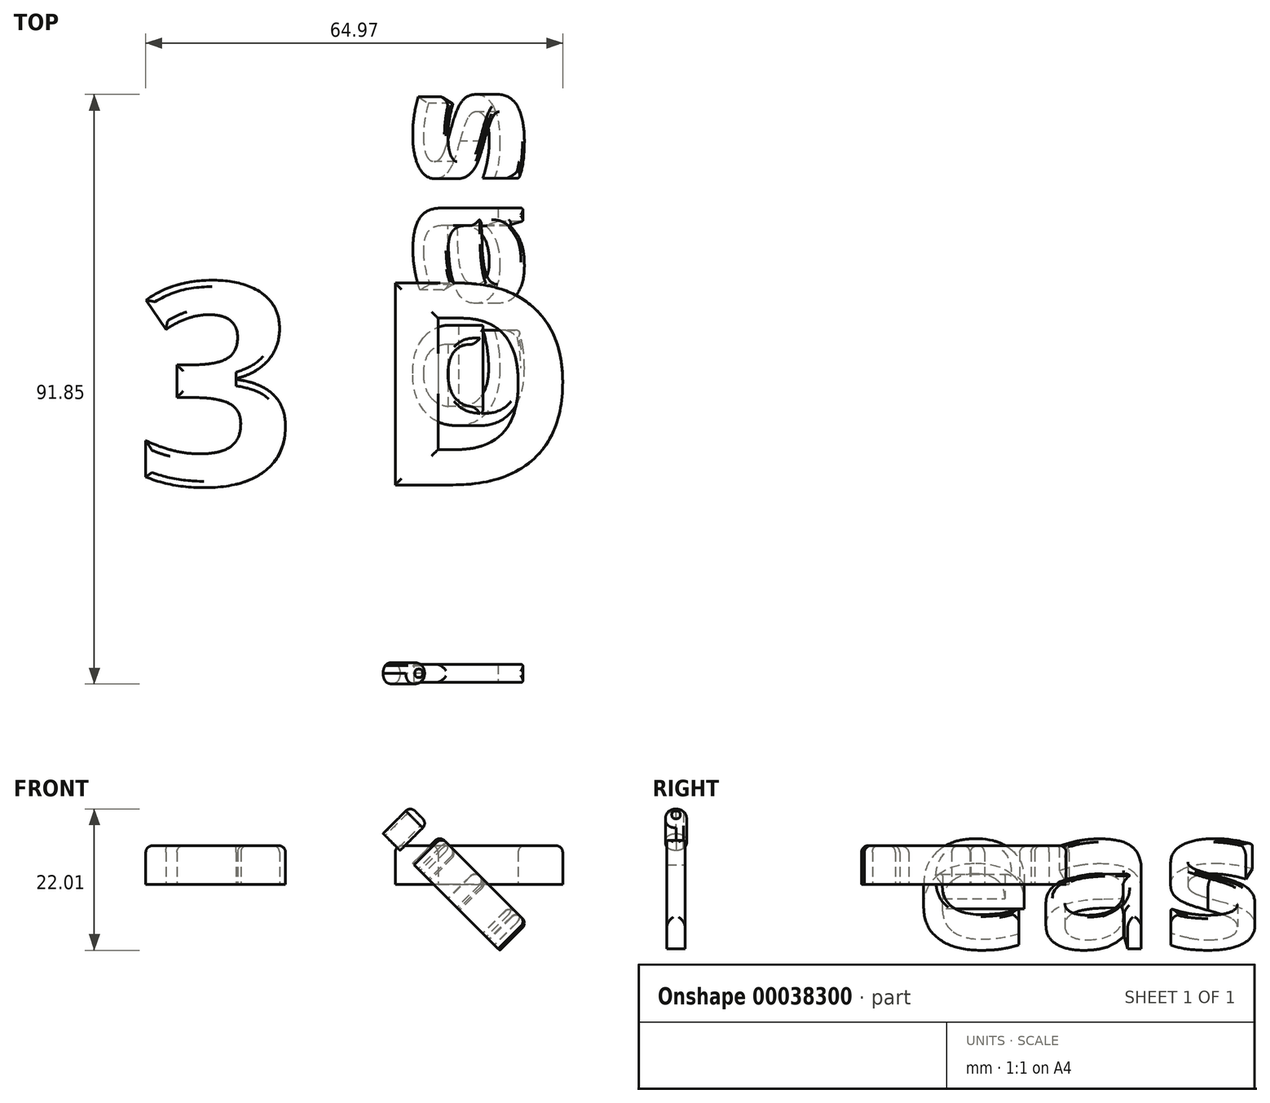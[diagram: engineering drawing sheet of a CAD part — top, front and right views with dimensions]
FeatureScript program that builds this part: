
annotation { "Feature Type Name" : "Feature", "Feature Type Description" : "" }
export const myFeature = defineFeature(function(context is Context, id is Id, definition is map)
    precondition{}
    {
        {
            var Q0;
            Q0=qCreatedBy(makeId("Top.planeOp"),FACE);
            var sketch = newSketch(context, id + "F0", { "sketchPlane" : qUnion([Q0])});
            skText(sketch, "E0", { "text": "3 D", "fontName": "OpenSans-Bold.ttf"});
            const initialGuessF0  = {"E0": [-0.06666, 0, 1, 0, 0.03172]};
            skSetInitialGuess(sketch, initialGuessF0);
            skSolve(sketch);
        }
        {
            var Q0;
            Q0=makeQuery(id+"F0.imprint","IMPRINT",FACE,{"disambiguationData":[TD([[makeQuery(id+"F0.imprint","IMPRINT",EDGE,{"derivedFrom":sQuery(id+"F0.wireOp",EDGE,"E0.sketch_text.stroke-0")}),-1.0]])]});
            var Q1;
            Q1=makeQuery(id+"F0.imprint","IMPRINT",FACE,{"disambiguationData":[TD([[makeQuery(id+"F0.imprint","IMPRINT",EDGE,{"derivedFrom":sQuery(id+"F0.wireOp",EDGE,"1949aad5-839d-4fb3-a845-ca18cb88f10a.sketch_text.stroke-0")}),-1.0]])]});
            var Q2;
            Q2=makeQuery(id+"F0.imprint","IMPRINT",FACE,{"disambiguationData":[TD([[makeQuery(id+"F0.imprint","IMPRINT",EDGE,{"derivedFrom":sQuery(id+"F0.wireOp",EDGE,"1949aad5-839d-4fb3-a845-ca18cb88f10a.sketch_text.stroke-9")}),-1.0]])]});
            var Q3;
            Q3=makeQuery(id+"F0.imprint","IMPRINT",FACE,{"disambiguationData":[TD([[makeQuery(id+"F0.imprint","IMPRINT",EDGE,{"derivedFrom":sQuery(id+"F0.wireOp",EDGE,"1949aad5-839d-4fb3-a845-ca18cb88f10a.sketch_text.stroke-41")}),-1.0]])]});
            var Q4;
            Q4=makeQuery(id+"F0.imprint","IMPRINT",FACE,{"disambiguationData":[TD([[makeQuery(id+"F0.imprint","IMPRINT",EDGE,{"derivedFrom":sQuery(id+"F0.wireOp",EDGE,"E0.sketch_text.stroke-27")}),-1.0]])]});
            var Q5;
            Q5=makeQuery(id+"F0.imprint","IMPRINT",FACE,{"disambiguationData":[TD([[makeQuery(id+"F0.imprint","IMPRINT",EDGE,{"derivedFrom":sQuery(id+"F0.wireOp",EDGE,"1949aad5-839d-4fb3-a845-ca18cb88f10a.sketch_text.stroke-16")}),-1.0]])]});
            extrude(context, id + "F1", {"entities" : qUnion([Q0, Q1, Q2, Q3, Q4, Q5]), "depth" : 6 * mm});
        }
        {
            var Q0;
            Q0=makeQuery(id+"F1.opExtrude","CAP_EDGE",EDGE,{"disambiguationData":[OSD([sQuery(id+"F0.wireOp",EDGE,"E0.sketch_text.stroke-30")])],"isStart":false});
            cPlane(context, id + "F2", {"entities" : qUnion([Q0]), "cplaneType" : CPlaneType.LINE_ANGLE, "offset" : 150 * mm, "angle" : 45 * degree, "width" : 150 * mm, "height" : 150 * mm});
        }
        {
            var Q0;
            Q0=qCreatedBy(id+"F2.planeOp",FACE);
            var sketch = newSketch(context, id + "F3", { "sketchPlane" : qUnion([Q0])});
            skText(sketch, "E1", { "text": "i", "fontName": "OpenSans-Regular.ttf"});
            skText(sketch, "E2", { "text": "eas", "fontName": "OpenSans-Regular.ttf"});
            const initialGuessF3  = {"E1": [-0.03374, 0, 1, 0, 0.0249], "E2": [0.0073, 0, 1, 0, 0.0249]};
            skSetInitialGuess(sketch, initialGuessF3);
            skSolve(sketch);
        }
        {
            var Q0;
            Q0=qSketchRegion(id+"F3",true);
            extrude(context, id + "F4", {"entities" : qUnion([Q0]), "depth" : 6 * mm});
        }
        {
            var Q0;
            Q0=makeQuery(id+"F1.opExtrude","CAP_EDGE",EDGE,{"disambiguationData":[OSD([sQuery(id+"F0.wireOp",EDGE,"E0.sketch_text.stroke-6")])],"isStart":false});
            var Q1;
            Q1=makeQuery(id+"F1.opExtrude","CAP_EDGE",EDGE,{"disambiguationData":[OSD([sQuery(id+"F0.wireOp",EDGE,"E0.sketch_text.stroke-0")])],"isStart":false});
            var Q2;
            Q2=makeQuery(id+"F1.opExtrude","CAP_EDGE",EDGE,{"disambiguationData":[OSD([sQuery(id+"F0.wireOp",EDGE,"E0.sketch_text.stroke-23")])],"isStart":false});
            var Q3;
            Q3=makeQuery(id+"F1.opExtrude","CAP_EDGE",EDGE,{"disambiguationData":[OSD([sQuery(id+"F0.wireOp",EDGE,"E0.sketch_text.stroke-21")])],"isStart":false});
            var Q4;
            Q4=makeQuery(id+"F1.opExtrude","CAP_EDGE",EDGE,{"disambiguationData":[OSD([sQuery(id+"F0.wireOp",EDGE,"E0.sketch_text.stroke-16")])],"isStart":false});
            var Q5;
            Q5=makeQuery(id+"F1.opExtrude","CAP_EDGE",EDGE,{"disambiguationData":[OSD([sQuery(id+"F0.wireOp",EDGE,"E0.sketch_text.stroke-14")])],"isStart":false});
            var Q6;
            Q6=makeQuery(id+"F1.opExtrude","CAP_EDGE",EDGE,{"disambiguationData":[OSD([sQuery(id+"F0.wireOp",EDGE,"E0.sketch_text.stroke-8")])],"isStart":false});
            var Q7;
            Q7=makeQuery(id+"F1.opExtrude","CAP_EDGE",EDGE,{"disambiguationData":[OSD([sQuery(id+"F0.wireOp",EDGE,"E0.sketch_text.stroke-30")])],"isStart":false});
            var Q8;
            Q8=makeQuery(id+"F1.opExtrude","CAP_EDGE",EDGE,{"disambiguationData":[OSD([sQuery(id+"F0.wireOp",EDGE,"E0.sketch_text.stroke-31")])],"isStart":false});
            var Q9;
            Q9=makeQuery(id+"F1.opExtrude","CAP_EDGE",EDGE,{"disambiguationData":[OSD([sQuery(id+"F0.wireOp",EDGE,"E0.sketch_text.stroke-36")])],"isStart":false});
            var Q10;
            Q10=makeQuery(id+"F1.opExtrude","CAP_EDGE",EDGE,{"disambiguationData":[OSD([sQuery(id+"F0.wireOp",EDGE,"E0.sketch_text.stroke-35")])],"isStart":false});
            var Q11;
            Q11=makeQuery(id+"F4.opExtrude","CAP_FACE",FACE,{"disambiguationData":[OSD([sQuery(id+"F3.wireOp",EDGE,"E1.sketch_text.stroke-0"),sQuery(id+"F3.wireOp",EDGE,"E1.sketch_text.stroke-1"),sQuery(id+"F3.wireOp",EDGE,"E1.sketch_text.stroke-2"),sQuery(id+"F3.wireOp",EDGE,"E1.sketch_text.stroke-3")])],"isStart":false});
            var Q12;
            Q12=makeQuery(id+"F4.opExtrude","CAP_FACE",FACE,{"disambiguationData":[OSD([sQuery(id+"F3.wireOp",EDGE,"E1.sketch_text.stroke-4"),sQuery(id+"F3.wireOp",EDGE,"E1.sketch_text.stroke-5"),sQuery(id+"F3.wireOp",EDGE,"E1.sketch_text.stroke-6"),sQuery(id+"F3.wireOp",EDGE,"E1.sketch_text.stroke-7"),sQuery(id+"F3.wireOp",EDGE,"E1.sketch_text.stroke-8"),sQuery(id+"F3.wireOp",EDGE,"E1.sketch_text.stroke-9"),sQuery(id+"F3.wireOp",EDGE,"E1.sketch_text.stroke-10"),sQuery(id+"F3.wireOp",EDGE,"E1.sketch_text.stroke-11")])],"isStart":false});
            var Q13;
            Q13=makeQuery(id+"F4.opExtrude","CAP_FACE",FACE,{"disambiguationData":[OSD([sQuery(id+"F3.wireOp",EDGE,"E2.sketch_text.stroke-0"),sQuery(id+"F3.wireOp",EDGE,"E2.sketch_text.stroke-1"),sQuery(id+"F3.wireOp",EDGE,"E2.sketch_text.stroke-2"),sQuery(id+"F3.wireOp",EDGE,"E2.sketch_text.stroke-3"),sQuery(id+"F3.wireOp",EDGE,"E2.sketch_text.stroke-4"),sQuery(id+"F3.wireOp",EDGE,"E2.sketch_text.stroke-5"),sQuery(id+"F3.wireOp",EDGE,"E2.sketch_text.stroke-6"),sQuery(id+"F3.wireOp",EDGE,"E2.sketch_text.stroke-7"),sQuery(id+"F3.wireOp",EDGE,"E2.sketch_text.stroke-8"),sQuery(id+"F3.wireOp",EDGE,"E2.sketch_text.stroke-9"),sQuery(id+"F3.wireOp",EDGE,"E2.sketch_text.stroke-10"),sQuery(id+"F3.wireOp",EDGE,"E2.sketch_text.stroke-11"),sQuery(id+"F3.wireOp",EDGE,"E2.sketch_text.stroke-12"),sQuery(id+"F3.wireOp",EDGE,"E2.sketch_text.stroke-13"),sQuery(id+"F3.wireOp",EDGE,"E2.sketch_text.stroke-14"),sQuery(id+"F3.wireOp",EDGE,"E2.sketch_text.stroke-15"),sQuery(id+"F3.wireOp",EDGE,"E2.sketch_text.stroke-16"),sQuery(id+"F3.wireOp",EDGE,"E2.sketch_text.stroke-17"),sQuery(id+"F3.wireOp",EDGE,"E2.sketch_text.stroke-18")])],"isStart":false});
            var Q14;
            Q14=makeQuery(id+"F4.opExtrude","CAP_FACE",FACE,{"disambiguationData":[OSD([sQuery(id+"F3.wireOp",EDGE,"E2.sketch_text.stroke-19"),sQuery(id+"F3.wireOp",EDGE,"E2.sketch_text.stroke-20"),sQuery(id+"F3.wireOp",EDGE,"E2.sketch_text.stroke-21"),sQuery(id+"F3.wireOp",EDGE,"E2.sketch_text.stroke-22"),sQuery(id+"F3.wireOp",EDGE,"E2.sketch_text.stroke-23"),sQuery(id+"F3.wireOp",EDGE,"E2.sketch_text.stroke-24"),sQuery(id+"F3.wireOp",EDGE,"E2.sketch_text.stroke-25"),sQuery(id+"F3.wireOp",EDGE,"E2.sketch_text.stroke-26"),sQuery(id+"F3.wireOp",EDGE,"E2.sketch_text.stroke-27"),sQuery(id+"F3.wireOp",EDGE,"E2.sketch_text.stroke-28"),sQuery(id+"F3.wireOp",EDGE,"E2.sketch_text.stroke-29"),sQuery(id+"F3.wireOp",EDGE,"E2.sketch_text.stroke-30"),sQuery(id+"F3.wireOp",EDGE,"E2.sketch_text.stroke-31"),sQuery(id+"F3.wireOp",EDGE,"E2.sketch_text.stroke-32"),sQuery(id+"F3.wireOp",EDGE,"E2.sketch_text.stroke-33"),sQuery(id+"F3.wireOp",EDGE,"E2.sketch_text.stroke-34"),sQuery(id+"F3.wireOp",EDGE,"E2.sketch_text.stroke-35"),sQuery(id+"F3.wireOp",EDGE,"E2.sketch_text.stroke-36"),sQuery(id+"F3.wireOp",EDGE,"E2.sketch_text.stroke-37"),sQuery(id+"F3.wireOp",EDGE,"E2.sketch_text.stroke-38"),sQuery(id+"F3.wireOp",EDGE,"E2.sketch_text.stroke-39"),sQuery(id+"F3.wireOp",EDGE,"E2.sketch_text.stroke-40"),sQuery(id+"F3.wireOp",EDGE,"E2.sketch_text.stroke-41"),sQuery(id+"F3.wireOp",EDGE,"E2.sketch_text.stroke-42"),sQuery(id+"F3.wireOp",EDGE,"E2.sketch_text.stroke-43"),sQuery(id+"F3.wireOp",EDGE,"E2.sketch_text.stroke-44"),sQuery(id+"F3.wireOp",EDGE,"E2.sketch_text.stroke-45")])],"isStart":false});
            var Q15;
            Q15=makeQuery(id+"F4.opExtrude","CAP_FACE",FACE,{"disambiguationData":[OSD([sQuery(id+"F3.wireOp",EDGE,"E2.sketch_text.stroke-46"),sQuery(id+"F3.wireOp",EDGE,"E2.sketch_text.stroke-47"),sQuery(id+"F3.wireOp",EDGE,"E2.sketch_text.stroke-48"),sQuery(id+"F3.wireOp",EDGE,"E2.sketch_text.stroke-49"),sQuery(id+"F3.wireOp",EDGE,"E2.sketch_text.stroke-50"),sQuery(id+"F3.wireOp",EDGE,"E2.sketch_text.stroke-51"),sQuery(id+"F3.wireOp",EDGE,"E2.sketch_text.stroke-52"),sQuery(id+"F3.wireOp",EDGE,"E2.sketch_text.stroke-53"),sQuery(id+"F3.wireOp",EDGE,"E2.sketch_text.stroke-54"),sQuery(id+"F3.wireOp",EDGE,"E2.sketch_text.stroke-55"),sQuery(id+"F3.wireOp",EDGE,"E2.sketch_text.stroke-56"),sQuery(id+"F3.wireOp",EDGE,"E2.sketch_text.stroke-57"),sQuery(id+"F3.wireOp",EDGE,"E2.sketch_text.stroke-58"),sQuery(id+"F3.wireOp",EDGE,"E2.sketch_text.stroke-59"),sQuery(id+"F3.wireOp",EDGE,"E2.sketch_text.stroke-60"),sQuery(id+"F3.wireOp",EDGE,"E2.sketch_text.stroke-61"),sQuery(id+"F3.wireOp",EDGE,"E2.sketch_text.stroke-62"),sQuery(id+"F3.wireOp",EDGE,"E2.sketch_text.stroke-63"),sQuery(id+"F3.wireOp",EDGE,"E2.sketch_text.stroke-64"),sQuery(id+"F3.wireOp",EDGE,"E2.sketch_text.stroke-65"),sQuery(id+"F3.wireOp",EDGE,"E2.sketch_text.stroke-66"),sQuery(id+"F3.wireOp",EDGE,"E2.sketch_text.stroke-67"),sQuery(id+"F3.wireOp",EDGE,"E2.sketch_text.stroke-68"),sQuery(id+"F3.wireOp",EDGE,"E2.sketch_text.stroke-69"),sQuery(id+"F3.wireOp",EDGE,"E2.sketch_text.stroke-70")])],"isStart":false});
            fillet(context, id + "F5", {"entities" : qUnion([Q0, Q1, Q2, Q3, Q4, Q5, Q6, Q7, Q8, Q9, Q10, Q11, Q12, Q13, Q14, Q15]), "radius" : 1 * mm, "tangentPropagation" : true, "allowEdgeOverflow" : false});
        }
    });
